# Revit family: FlushPlateControlPanel-ToiletCisterns-Vitra-LoopOSeries-740-0585
name_source: partatom
category: Plumbing Fixtures
revit_build: Autodesk Revit 2017 (Build: 20160225_1515(x64)
units: mm (PartAtom-declared; Revit-internal decimal feet)

## family parameters
Cut with Voids When Loaded = No
Host = Face
OmniClass Number = 23.45.05.21.11
OmniClass Title = Water Closets
Part Type = Normal
Room Calculation Point = No
Round Connector Dimension = Use Diameter
Shared = Yes

## types (7) — shared parameters
BIMobject category = Toilet Cisterns
Brand = Vitra
CW Connection = No
Design country = Turkey
HW Connection = No
IFC Classification = Sanitary Terminal
Installation instructions = https://cdn.vitra.com.tr
Main Material = ABS Plastic
Manufacturer = Vitra
Manufacturer name = Vitra
Masterformat 2014 Code = 22 00 00
Masterformat 2014 Description = Plumbing
MountingType = Wall Mounted
NBS Referans Code = 35-05-65
NBS Referans Description = Sanitary, Cleaning, Maintenance And Storage Ff
Nominal Depth (mm) = 15 mm  [stored 0.0492126 ft]
Nominal Height (mm) = 165 mm  [stored 0.541339 ft]
Nominal Width (mm) = 244 mm  [stored 0.800525 ft]
OmniClass Code = 23-31 00 00
OmniClass Description = Plumbing Specific Products and Equipment
Product certification = https://vitraglobal.com
Product data url = https://www.vitraglobal.com
Product family = LoopO
Product group = WC Cisterns Control Panel
Technical description = https://www.vitraglobal.com
UNSPSC Code = 40141720
UNSPSC Description = Plumbing connectors
URL = https://www.vitra.com.tr
Uniclass 1.4 Code = L71111
Uniclass 1.4 Description = Packaged plumbing units
Uniclass 2.0 Code = SS-35-65
Uniclass 2.0 Description = Sanitary, Cleaning, Maintenance And Storage Ff&E Systems
Uniclass 2015 Code = Ac_10_40_67
Uniclass 2015 Name = Plumbing
Uniformat II Code = D20
Uniformat II Description = PLUMBING
Vent Connection = No
Warranty Period (Year) = 2 Years
Waste Connection = No
Weight Net (kg) = 0,500
Youtube = https://www.youtube.com
zero-valued in all types: Cost, Default Elevation

## per-type parameters (varying)
| type | Article No. (default) | Color | Description | Model | Product SKU | Secondary Material |
| WC_ToiletCisternsControlPanel-Vitra-LoopOSeries_740-0585 | 740-0585 | Matte Chrome | VitrA WC Cisterns Control Panel | 740-0585 | 740-0585 | MatteChrome |
| WC_ToiletCisternsControlPanel-Vitra-LoopOSeries_740-0511 | 740-0511 | Matte Black | VitrA WC Cisterns Control Panel | 740-0511 | 740-0511 | Matte Black |
| WC_ToiletCisternsControlPanel-Vitra-LoopOSeries_740-0580 | 740-0580 | High Gloss Chrome | VitrA WC Cisterns Control Panel | 740-0580 | 740-0580 | High Gloss Chrome |
| WC_ToiletCisternsControlPanel-Vitra-LoopOSeries_740-0500 | 740-0500 | High Gloss White | VitrA WC Cisterns Control Panel | 740-0500 | 740-0500 | High Gloss White |
| WC_ToiletCisternsControlPanel-Vitra-LoopOSeries_740-0586 | 740-0586 | Matte Chrome | VitrA WC Cisterns Control Panel, AntiFingerPrint | 740-0586 | 740-0586 | MatteChrome |
| WC_ToiletCisternsControlPanel-Vitra-LoopOSeries_740-0940 | 740-0940 | Chrome | VitrA WC Cisterns Control Panel, | 740-0940 | 740-0940 | Chrome |
| WC_ToiletCisternsControlPanel-Vitra-LoopOSeries_740-0585IND | 740-0585IND | Matte Chrome | VitrA WC Cisterns Control Panel | 740-0585IND | 740-0585IND | MatteChrome |

note: [stored X ft] marks values corroborated as IEEE doubles in the binary element streams (Revit-internal decimal feet)

## geometry (parser evidence)
native form markers: Sweep x3
no freeform markers — native parametric forms only
